# Revit family: Louver-Channel_Frame-Carnes-Rectangular-Sight_Proof_FYKB
name_source: partatom
category: Air Terminals
revit_build: Autodesk Revit MEP 2012 (Build: 20110916_2132(x64)
units: mm (PartAtom-declared; Revit-internal decimal feet)

## types (1)
- (See Type Catalog)
    04 CSI = 08 91 00
    95 CSI = 10200
    Airflow = 0 CFM
    Assembly Code = D3090700
    Blade Material = Aluminum - Carnes - Extruded
    Catalog URL = http://www.carnes.com
    Connector Description 1 = Duct Connetor
    Default Elevation = 48"
    Description = Sight Proof Louvers
    Frame Material = Aluminum - Carnes - Extruded
    Free Area = 0 SF
    Free Area Note = See Spec Sheet URL
    Louver Height = 120"
    Louver Length = 2 5/32"
    Louver Width = 84"
    Manufacturer = Carnes Company
    Manufacturer Fax = 608-845-6470
    Maximum Horinzontal Size = 120"W x 84"H
    Maximum Vertical Size = 84"W x 120"H
    Meets Building Code Standards = Licensed to bear the AMCA seal
    Minimum Size = 12"W x 12"H
    Model = FYKB
    Outside Height = 122"
    Outside Width = 86"
    Pressure Drop = 0.00 Pa
    Product Line = Sight Proof Louvers
    Product Page URL = http://www.carnes.com
    Specifications  URL = http://www.carnes.com
    Subcategory = Louvers and Dampers
    URL = http://www.carnes.com
    ecoScorecard Product Page = http://ecoscorecard.com

## geometry (parser evidence)
native form markers: Blend x1, Sweep x5
no freeform markers — native parametric forms only
